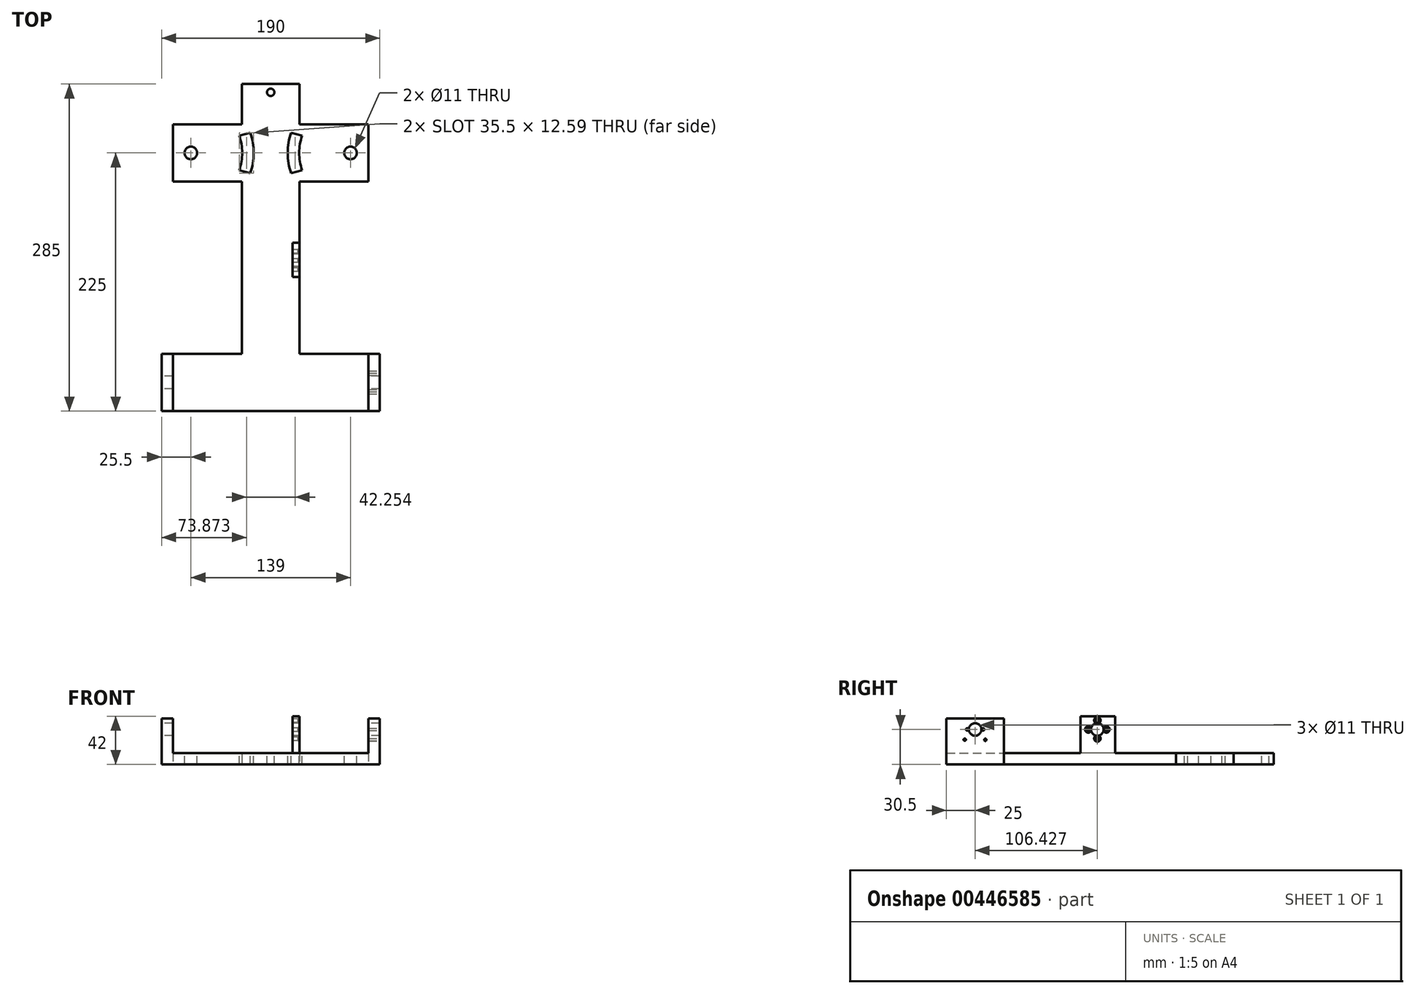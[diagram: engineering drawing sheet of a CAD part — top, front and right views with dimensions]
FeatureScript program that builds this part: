
annotation { "Feature Type Name" : "Feature", "Feature Type Description" : "" }
export const myFeature = defineFeature(function(context is Context, id is Id, definition is map)
    precondition{}
    {
        {
            var Q0;
            Q0=qCreatedBy(makeId("Top.planeOp"),FACE);
            var sketch = newSketch(context, id + "F0", { "sketchPlane" : qUnion([Q0])});
            skLineSegment(sketch, "E0.bottom", {"start": v(25, 75) * mm, "end": v(-25, 75) * mm});
            skLineSegment(sketch, "E0.top", {"start": v(25, -75) * mm, "end": v(-25, -75) * mm});
            skLineSegment(sketch, "E0.left", {"start": v(25, 75) * mm, "end": v(25, -75) * mm});
            skLineSegment(sketch, "E0.right", {"start": v(-25, 75) * mm, "end": v(-25, -75) * mm});
            skPoint(sketch, "E0.middle", {"position": v(0, 0) * mm});
            skLineSegment(sketch, "E1.top", {"start": v(25, 125) * mm, "end": v(-25, 125) * mm});
            skLineSegment(sketch, "E1.left", {"start": v(25, 75) * mm, "end": v(25, 125) * mm});
            skLineSegment(sketch, "E1.right", {"start": v(-25, 75) * mm, "end": v(-25, 125) * mm});
            skLineSegment(sketch, "E2.bottom", {"start": v(25, 75) * mm, "end": v(85, 75) * mm});
            skLineSegment(sketch, "E2.top", {"start": v(25, 125) * mm, "end": v(85, 125) * mm});
            skLineSegment(sketch, "E2.right", {"start": v(85, 75) * mm, "end": v(85, 125) * mm});
            skLineSegment(sketch, "E3.bottom", {"start": v(-25, 75) * mm, "end": v(-85, 75) * mm});
            skLineSegment(sketch, "E3.top", {"start": v(-25, 125) * mm, "end": v(-85, 125) * mm});
            skLineSegment(sketch, "E3.right", {"start": v(-85, 75) * mm, "end": v(-85, 125) * mm});
            skLineSegment(sketch, "E4.bottom", {"start": v(-25, -75) * mm, "end": v(-95, -75) * mm});
            skLineSegment(sketch, "E4.top", {"start": v(-25, -125) * mm, "end": v(-95, -125) * mm});
            skLineSegment(sketch, "E4.left", {"start": v(-25, -75) * mm, "end": v(-25, -125) * mm});
            skLineSegment(sketch, "E4.right", {"start": v(-95, -75) * mm, "end": v(-95, -125) * mm});
            skLineSegment(sketch, "E5.bottom", {"start": v(25, -75) * mm, "end": v(95, -75) * mm});
            skLineSegment(sketch, "E5.top", {"start": v(25, -125) * mm, "end": v(95, -125) * mm});
            skLineSegment(sketch, "E5.left", {"start": v(25, -75) * mm, "end": v(25, -125) * mm});
            skLineSegment(sketch, "E5.right", {"start": v(95, -75) * mm, "end": v(95, -125) * mm});
            skLineSegment(sketch, "E6.bottom", {"start": v(-25, -75) * mm, "end": v(25, -75) * mm});
            skLineSegment(sketch, "E6.top", {"start": v(-25, -125) * mm, "end": v(25, -125) * mm});
            skLineSegment(sketch, "E7.bottom", {"start": v(-25, 125) * mm, "end": v(25, 125) * mm});
            skLineSegment(sketch, "E7.top", {"start": v(-25, 160) * mm, "end": v(25, 160) * mm});
            skLineSegment(sketch, "E7.left", {"start": v(-25, 125) * mm, "end": v(-25, 160) * mm});
            skLineSegment(sketch, "E7.right", {"start": v(25, 125) * mm, "end": v(25, 160) * mm});
            skSolve(sketch);
        }
        {
            var Q0;
            Q0 = qSketchRegion(id + "F0", true);
            extrude(context, id + "F1", {"entities" : qUnion([Q0]), "depth" : 10 * mm});
        }
        {
            var Q0;
            Q0=makeQuery(id+"F1.opExtrude","CAP_FACE",FACE,{"disambiguationData":[OSD([sQuery(id+"F0.wireOp",EDGE,"E0.left"),sQuery(id+"F0.wireOp",EDGE,"E0.right"),sQuery(id+"F0.wireOp",EDGE,"E1.top"),sQuery(id+"F0.wireOp",EDGE,"E2.bottom"),sQuery(id+"F0.wireOp",EDGE,"E2.top"),sQuery(id+"F0.wireOp",EDGE,"E2.right"),sQuery(id+"F0.wireOp",EDGE,"E3.bottom"),sQuery(id+"F0.wireOp",EDGE,"E3.top"),sQuery(id+"F0.wireOp",EDGE,"E3.right"),sQuery(id+"F0.wireOp",EDGE,"E4.bottom"),sQuery(id+"F0.wireOp",EDGE,"E4.top"),sQuery(id+"F0.wireOp",EDGE,"E4.right"),sQuery(id+"F0.wireOp",EDGE,"E5.bottom"),sQuery(id+"F0.wireOp",EDGE,"E5.top"),sQuery(id+"F0.wireOp",EDGE,"E5.right"),sQuery(id+"F0.wireOp",EDGE,"E6.top")])],"isStart":false});
            var sketch = newSketch(context, id + "F2", { "sketchPlane" : qUnion([Q0])});
            skLineSegment(sketch, "E8.bottom", {"start": v(-95, -125) * mm, "end": v(-85, -125) * mm});
            skLineSegment(sketch, "E8.top", {"start": v(-95, -75) * mm, "end": v(-85, -75) * mm});
            skLineSegment(sketch, "E8.left", {"start": v(-95, -125) * mm, "end": v(-95, -75) * mm});
            skLineSegment(sketch, "E8.right", {"start": v(-85, -125) * mm, "end": v(-85, -75) * mm});
            skLineSegment(sketch, "E9.bottom", {"start": v(95, -75) * mm, "end": v(85, -75) * mm});
            skLineSegment(sketch, "E9.top", {"start": v(95, -125) * mm, "end": v(85, -125) * mm});
            skLineSegment(sketch, "E9.left", {"start": v(95, -75) * mm, "end": v(95, -125) * mm});
            skLineSegment(sketch, "E9.right", {"start": v(85, -75) * mm, "end": v(85, -125) * mm});
            skSolve(sketch);
        }
        {
            var Q0;
            Q0 = qSketchRegion(id + "F2", true);
            extrude(context, id + "F3", {"entities" : qUnion([Q0]), "operationType" : NewBodyOperationType.ADD, "depth" : 30 * mm});
        }
        {
            var Q0;
            Q0=makeQuery(id+"F3.boolean.opBoolean","MERGE",FACE,{"derivedFrom":[makeQuery(id+"F1.opExtrude","SWEPT_FACE",FACE,{"disambiguationData":[OSD([sQuery(id+"F0.wireOp",EDGE,"E4.right")])]}),makeQuery(id+"F3.opExtrude","SWEPT_FACE",FACE,{"disambiguationData":[OSD([sQuery(id+"F2.wireOp",EDGE,"E8.left")])]})]});
            var sketch = newSketch(context, id + "F4", { "sketchPlane" : qUnion([Q0])});
            skCircle(sketch, "E10", {"center": v(100, 30.5) * mm, "radius": 5.5 * mm});
            skPoint(sketch, "E10.centerSnap0", {"position": v(100, 0) * mm});
            skSolve(sketch);
        }
        {
            var Q0;
            Q0 = qSketchRegion(id + "F4", true);
            extrude(context, id + "F5", {"entities" : qUnion([Q0]), "operationType" : NewBodyOperationType.REMOVE, "endBound" : BoundingType.THROUGH_ALL, "oppositeDirection" : true, "depth" : 267 * mm});
        }
        {
            var Q0;
            Q0=makeQuery(id+"F1.opExtrude","CAP_FACE",FACE,{"disambiguationData":[OSD([sQuery(id+"F0.wireOp",EDGE,"E0.left"),sQuery(id+"F0.wireOp",EDGE,"E0.right"),sQuery(id+"F0.wireOp",EDGE,"E2.bottom"),sQuery(id+"F0.wireOp",EDGE,"E2.top"),sQuery(id+"F0.wireOp",EDGE,"E2.right"),sQuery(id+"F0.wireOp",EDGE,"E3.bottom"),sQuery(id+"F0.wireOp",EDGE,"E3.top"),sQuery(id+"F0.wireOp",EDGE,"E3.right"),sQuery(id+"F0.wireOp",EDGE,"E4.bottom"),sQuery(id+"F0.wireOp",EDGE,"E4.top"),sQuery(id+"F0.wireOp",EDGE,"E4.right"),sQuery(id+"F0.wireOp",EDGE,"E5.bottom"),sQuery(id+"F0.wireOp",EDGE,"E5.top"),sQuery(id+"F0.wireOp",EDGE,"E5.right"),sQuery(id+"F0.wireOp",EDGE,"E6.top"),sQuery(id+"F0.wireOp",EDGE,"E7.top"),sQuery(id+"F0.wireOp",EDGE,"E7.left"),sQuery(id+"F0.wireOp",EDGE,"E7.right")])],"isStart":false});
            var sketch = newSketch(context, id + "F6", { "sketchPlane" : qUnion([Q0])});
            skCircle(sketch, "E11", {"center": v(0, 152.82) * mm, "radius": 3.18 * mm});
            skPoint(sketch, "E11.centerSnap0", {"position": v(25, 142.5) * mm});
            skSolve(sketch);
        }
        {
            var Q0;
            Q0 = qSketchRegion(id + "F6", true);
            extrude(context, id + "F7", {"entities" : qUnion([Q0]), "operationType" : NewBodyOperationType.REMOVE, "endBound" : BoundingType.THROUGH_ALL, "oppositeDirection" : true, "depth" : 25 * mm});
        }
        {
            var Q0;
            Q0=makeQuery(id+"F1.opExtrude","CAP_FACE",FACE,{"disambiguationData":[OSD([sQuery(id+"F0.wireOp",EDGE,"E0.left"),sQuery(id+"F0.wireOp",EDGE,"E0.right"),sQuery(id+"F0.wireOp",EDGE,"E2.bottom"),sQuery(id+"F0.wireOp",EDGE,"E2.top"),sQuery(id+"F0.wireOp",EDGE,"E2.right"),sQuery(id+"F0.wireOp",EDGE,"E3.bottom"),sQuery(id+"F0.wireOp",EDGE,"E3.top"),sQuery(id+"F0.wireOp",EDGE,"E3.right"),sQuery(id+"F0.wireOp",EDGE,"E4.bottom"),sQuery(id+"F0.wireOp",EDGE,"E4.top"),sQuery(id+"F0.wireOp",EDGE,"E4.right"),sQuery(id+"F0.wireOp",EDGE,"E5.bottom"),sQuery(id+"F0.wireOp",EDGE,"E5.top"),sQuery(id+"F0.wireOp",EDGE,"E5.right"),sQuery(id+"F0.wireOp",EDGE,"E6.top"),sQuery(id+"F0.wireOp",EDGE,"E7.top"),sQuery(id+"F0.wireOp",EDGE,"E7.left"),sQuery(id+"F0.wireOp",EDGE,"E7.right")])],"isStart":false});
            var sketch = newSketch(context, id + "F8", { "sketchPlane" : qUnion([Q0])});
            skCircle(sketch, "E12", {"center": v(-69.5, 100) * mm, "radius": 5.5 * mm});
            skPoint(sketch, "E12.centerSnap0", {"position": v(-85, 100) * mm});
            skSolve(sketch);
        }
        {
            var Q0;
            Q0 = qSketchRegion(id + "F8", true);
            extrude(context, id + "F9", {"entities" : qUnion([Q0]), "operationType" : NewBodyOperationType.REMOVE, "endBound" : BoundingType.THROUGH_ALL, "oppositeDirection" : true, "depth" : 25 * mm});
        }
        {
            var Q0;
            Q0=makeQuery(id+"F1.opExtrude","CAP_FACE",FACE,{"disambiguationData":[OSD([sQuery(id+"F0.wireOp",EDGE,"E0.left"),sQuery(id+"F0.wireOp",EDGE,"E0.right"),sQuery(id+"F0.wireOp",EDGE,"E2.bottom"),sQuery(id+"F0.wireOp",EDGE,"E2.top"),sQuery(id+"F0.wireOp",EDGE,"E2.right"),sQuery(id+"F0.wireOp",EDGE,"E3.bottom"),sQuery(id+"F0.wireOp",EDGE,"E3.top"),sQuery(id+"F0.wireOp",EDGE,"E3.right"),sQuery(id+"F0.wireOp",EDGE,"E4.bottom"),sQuery(id+"F0.wireOp",EDGE,"E4.top"),sQuery(id+"F0.wireOp",EDGE,"E4.right"),sQuery(id+"F0.wireOp",EDGE,"E5.bottom"),sQuery(id+"F0.wireOp",EDGE,"E5.top"),sQuery(id+"F0.wireOp",EDGE,"E5.right"),sQuery(id+"F0.wireOp",EDGE,"E6.top"),sQuery(id+"F0.wireOp",EDGE,"E7.top"),sQuery(id+"F0.wireOp",EDGE,"E7.left"),sQuery(id+"F0.wireOp",EDGE,"E7.right")])],"isStart":false});
            var sketch = newSketch(context, id + "F10", { "sketchPlane" : qUnion([Q0])});
            skCircle(sketch, "E13", {"center": v(69.5, 100) * mm, "radius": 5.5 * mm});
            skPoint(sketch, "E13.centerSnap0", {"position": v(85, 100) * mm});
            skSolve(sketch);
        }
        {
            var Q0;
            Q0 = qSketchRegion(id + "F10", true);
            extrude(context, id + "F11", {"entities" : qUnion([Q0]), "operationType" : NewBodyOperationType.REMOVE, "endBound" : BoundingType.THROUGH_ALL, "oppositeDirection" : true, "depth" : 25 * mm});
        }
        {
            var Q0;
            Q0=makeQuery(id+"F1.opExtrude","CAP_FACE",FACE,{"disambiguationData":[OSD([sQuery(id+"F0.wireOp",EDGE,"E0.left"),sQuery(id+"F0.wireOp",EDGE,"E0.right"),sQuery(id+"F0.wireOp",EDGE,"E2.bottom"),sQuery(id+"F0.wireOp",EDGE,"E2.top"),sQuery(id+"F0.wireOp",EDGE,"E2.right"),sQuery(id+"F0.wireOp",EDGE,"E3.bottom"),sQuery(id+"F0.wireOp",EDGE,"E3.top"),sQuery(id+"F0.wireOp",EDGE,"E3.right"),sQuery(id+"F0.wireOp",EDGE,"E4.bottom"),sQuery(id+"F0.wireOp",EDGE,"E4.top"),sQuery(id+"F0.wireOp",EDGE,"E4.right"),sQuery(id+"F0.wireOp",EDGE,"E5.bottom"),sQuery(id+"F0.wireOp",EDGE,"E5.top"),sQuery(id+"F0.wireOp",EDGE,"E5.right"),sQuery(id+"F0.wireOp",EDGE,"E6.top"),sQuery(id+"F0.wireOp",EDGE,"E7.top"),sQuery(id+"F0.wireOp",EDGE,"E7.left"),sQuery(id+"F0.wireOp",EDGE,"E7.right")])],"isStart":false});
            var sketch = newSketch(context, id + "F12", { "sketchPlane" : qUnion([Q0])});
            skArc(sketch, "E14", {"start": v(27.42, 85) * mm, "mid": v(24.83, 100) * mm, "end": v(27.42, 115) * mm});
            skArc(sketch, "E15.0", {"start": v(17.8, 82.25) * mm, "mid": v(14.83, 100) * mm, "end": v(17.8, 117.75) * mm});
            skLineSegment(sketch, "E16", {"start": v(27.42, 85) * mm, "end": v(17.8, 82.25) * mm});
            skLineSegment(sketch, "E17", {"start": v(27.42, 115) * mm, "end": v(17.8, 117.75) * mm});
            skArc(sketch, "E18.MirrorCS", {"start": v(-17.8, 82.25) * mm, "mid": v(-14.83, 100) * mm, "end": v(-17.8, 117.75) * mm});
            skArc(sketch, "E19.MirrorCS", {"start": v(-27.42, 85) * mm, "mid": v(-24.83, 100) * mm, "end": v(-27.42, 115) * mm});
            skLineSegment(sketch, "E20.MirrorCS", {"start": v(-27.42, 85) * mm, "end": v(-17.8, 82.25) * mm});
            skLineSegment(sketch, "E21.MirrorCS", {"start": v(-27.42, 115) * mm, "end": v(-17.8, 117.75) * mm});
            skSolve(sketch);
        }
        {
            var Q0;
            Q0 = qSketchRegion(id + "F12", true);
            extrude(context, id + "F13", {"entities" : qUnion([Q0]), "operationType" : NewBodyOperationType.REMOVE, "endBound" : BoundingType.THROUGH_ALL, "oppositeDirection" : true, "depth" : 25 * mm});
        }
        {
            var Q0;
            Q0=makeQuery(id+"F12.imprint","IMPRINT",FACE,{"disambiguationData":[TD([[makeQuery(id+"F12.imprint","IMPRINT",EDGE,{"derivedFrom":sQuery(id+"F12.wireOp",EDGE,"E14")}),-1.0]])]});
            var sketch = newSketch(context, id + "F14", { "sketchPlane" : qUnion([Q0])});
            skLineSegment(sketch, "E22.bottom", {"start": v(19, 21.84) * mm, "end": v(25, 21.84) * mm});
            skLineSegment(sketch, "E22.top", {"start": v(19, -8.16) * mm, "end": v(25, -8.16) * mm});
            skLineSegment(sketch, "E22.left", {"start": v(25, 21.84) * mm, "end": v(25, -8.16) * mm});
            skLineSegment(sketch, "E22.right", {"start": v(19, 21.84) * mm, "end": v(19, -8.16) * mm});
            skSolve(sketch);
        }
        {
            var Q0;
            Q0 = qSketchRegion(id + "F14", true);
            extrude(context, id + "F15", {"entities" : qUnion([Q0]), "operationType" : NewBodyOperationType.ADD, "depth" : 32 * mm});
        }
        {
            var Q0;
            Q0=makeQuery(id+"F15.opExtrude","SWEPT_FACE",FACE,{"disambiguationData":[OSD([sQuery(id+"F14.wireOp",EDGE,"E22.right")])]});
            var sketch = newSketch(context, id + "F16", { "sketchPlane" : qUnion([Q0])});
            skPoint(sketch, "E23", {"position": v(-6.43, 30.5) * mm});
            skCircle(sketch, "E24", {"center": v(-6.43, 30.5) * mm, "radius": 5.5 * mm});
            skSolve(sketch);
        }
        {
            var Q0;
            Q0=makeQuery(id+"F16.imprint","IMPRINT",FACE,{"disambiguationData":[TD([[makeQuery(id+"F16.imprint","IMPRINT",EDGE,{"derivedFrom":sQuery(id+"F16.wireOp",EDGE,"E24")}),1.0]])]});
            extrude(context, id + "F17", {"entities" : qUnion([Q0]), "operationType" : NewBodyOperationType.REMOVE, "endBound" : BoundingType.THROUGH_ALL, "oppositeDirection" : true, "depth" : 25 * mm});
        }
        {
            var Q0;
            Q0=makeQuery(id+"F15.boolean.opBoolean","MERGE",FACE,{"derivedFrom":[makeQuery(id+"F1.opExtrude","SWEPT_FACE",FACE,{"disambiguationData":[OSD([sQuery(id+"F0.wireOp",EDGE,"E0.left")])]}),makeQuery(id+"F15.opExtrude","SWEPT_FACE",FACE,{"disambiguationData":[OSD([sQuery(id+"F14.wireOp",EDGE,"E22.left")])]})]});
            var sketch = newSketch(context, id + "F18", { "sketchPlane" : qUnion([Q0])});
            skPoint(sketch, "E25", {"position": v(6.43, 30.5) * mm});
            skPoint(sketch, "E26", {"position": v(6.43, 38.4) * mm});
            skPoint(sketch, "E27", {"position": v(14.33, 30.5) * mm});
            skPoint(sketch, "E28", {"position": v(6.43, 22.6) * mm});
            skPoint(sketch, "E29", {"position": v(-1.47, 30.5) * mm});
            skLineSegment(sketch, "E30", {"start": v(6.43, 30.5) * mm, "end": v(6.43, 18.7) * mm});
            skSolve(sketch);
        }
        {
            var Q0;
            Q0=sQuery(id+"F18.wireOp",VERTEX,"E26");
            var Q1;
            Q1=sQuery(id+"F18.wireOp",VERTEX,"E27");
            var Q2;
            Q2=sQuery(id+"F18.wireOp",VERTEX,"E28");
            var Q3;
            Q3=sQuery(id+"F18.wireOp",VERTEX,"E29");
            var Q4;
            Q4=makeQuery(id+"F1.opExtrude","SWEPT_BODY",BODY,{"disambiguationData":[OSD([sQuery(id+"F0.wireOp",EDGE,"E0.left"),sQuery(id+"F0.wireOp",EDGE,"E0.right"),sQuery(id+"F0.wireOp",EDGE,"E2.bottom"),sQuery(id+"F0.wireOp",EDGE,"E2.top"),sQuery(id+"F0.wireOp",EDGE,"E2.right"),sQuery(id+"F0.wireOp",EDGE,"E3.bottom"),sQuery(id+"F0.wireOp",EDGE,"E3.top"),sQuery(id+"F0.wireOp",EDGE,"E3.right"),sQuery(id+"F0.wireOp",EDGE,"E4.bottom"),sQuery(id+"F0.wireOp",EDGE,"E4.top"),sQuery(id+"F0.wireOp",EDGE,"E4.right"),sQuery(id+"F0.wireOp",EDGE,"E5.bottom"),sQuery(id+"F0.wireOp",EDGE,"E5.top"),sQuery(id+"F0.wireOp",EDGE,"E5.right"),sQuery(id+"F0.wireOp",EDGE,"E6.top"),sQuery(id+"F0.wireOp",EDGE,"E7.top"),sQuery(id+"F0.wireOp",EDGE,"E7.left"),sQuery(id+"F0.wireOp",EDGE,"E7.right")])]});
            hole(context, id + "F19", {"style" : HoleStyle.C_SINK, "endStyle" : HoleEndStyle.THROUGH, "holeDiameter" : 3.1 * mm, "cSinkDiameter" : 5.6 * mm, "cSinkAngle" : 90 * degree, "isTappedThrough" : true, "tappedDepth" : 12 * mm, "tapClearance" : 3, "locations" : qUnion([Q0, Q1, Q2, Q3]), "scope" : qUnion([Q4])});
        }
        {
            var Q0;
            Q0=makeQuery(id+"F3.boolean.opBoolean","MERGE",FACE,{"derivedFrom":[makeQuery(id+"F1.opExtrude","SWEPT_FACE",FACE,{"disambiguationData":[OSD([sQuery(id+"F0.wireOp",EDGE,"E5.right")])]}),makeQuery(id+"F3.opExtrude","SWEPT_FACE",FACE,{"disambiguationData":[OSD([sQuery(id+"F2.wireOp",EDGE,"E9.left")])]})]});
            var sketch = newSketch(context, id + "F20", { "sketchPlane" : qUnion([Q0])});
            skPoint(sketch, "E31", {"position": v(-100, 30.5) * mm});
            skPoint(sketch, "E32", {"position": v(-92.9, 30.5) * mm});
            skPoint(sketch, "E33", {"position": v(-107.1, 30.5) * mm});
            skCircle(sketch, "E34", {"center": v(-100, 30.5) * mm, "radius": 6.2 * mm});
            skCircle(sketch, "E35", {"center": v(-100, 30.5) * mm, "radius": 8 * mm});
            skCircle(sketch, "E36", {"center": v(-100, 30.5) * mm, "radius": 11 * mm});
            skCircle(sketch, "E37", {"center": v(-100, 30.5) * mm, "radius": 12.7 * mm});
            skPoint(sketch, "E38", {"position": v(-91.09, 21.45) * mm});
            skPoint(sketch, "E39", {"position": v(-109.05, 21.59) * mm});
            skPoint(sketch, "E40", {"position": v(-108.91, 39.55) * mm});
            skPoint(sketch, "E41", {"position": v(-90.95, 39.41) * mm});
            skSolve(sketch);
        }
        {
            var Q0;
            Q0=sQuery(id+"F20.wireOp",VERTEX,"E33");
            var Q1;
            Q1=sQuery(id+"F20.wireOp",VERTEX,"E32");
            var Q2;
            Q2=sQuery(id+"F20.wireOp",VERTEX,"E38");
            var Q3;
            Q3=sQuery(id+"F20.wireOp",VERTEX,"E39");
            var Q4;
            Q4=makeQuery(id+"F1.opExtrude","SWEPT_BODY",BODY,{"disambiguationData":[OSD([sQuery(id+"F0.wireOp",EDGE,"E0.left"),sQuery(id+"F0.wireOp",EDGE,"E0.right"),sQuery(id+"F0.wireOp",EDGE,"E2.bottom"),sQuery(id+"F0.wireOp",EDGE,"E2.top"),sQuery(id+"F0.wireOp",EDGE,"E2.right"),sQuery(id+"F0.wireOp",EDGE,"E3.bottom"),sQuery(id+"F0.wireOp",EDGE,"E3.top"),sQuery(id+"F0.wireOp",EDGE,"E3.right"),sQuery(id+"F0.wireOp",EDGE,"E4.bottom"),sQuery(id+"F0.wireOp",EDGE,"E4.top"),sQuery(id+"F0.wireOp",EDGE,"E4.right"),sQuery(id+"F0.wireOp",EDGE,"E5.bottom"),sQuery(id+"F0.wireOp",EDGE,"E5.top"),sQuery(id+"F0.wireOp",EDGE,"E5.right"),sQuery(id+"F0.wireOp",EDGE,"E6.top"),sQuery(id+"F0.wireOp",EDGE,"E7.top"),sQuery(id+"F0.wireOp",EDGE,"E7.left"),sQuery(id+"F0.wireOp",EDGE,"E7.right")])]});
            hole(context, id + "F21", {"style" : HoleStyle.SIMPLE, "endStyle" : HoleEndStyle.BLIND, "holeDiameter" : 2 * mm, "holeDepth" : 30 * mm, "isTappedThrough" : true, "tappedDepth" : 12 * mm, "tapClearance" : 3, "locations" : qUnion([Q0, Q1, Q2, Q3]), "scope" : qUnion([Q4])});
        }
    });
